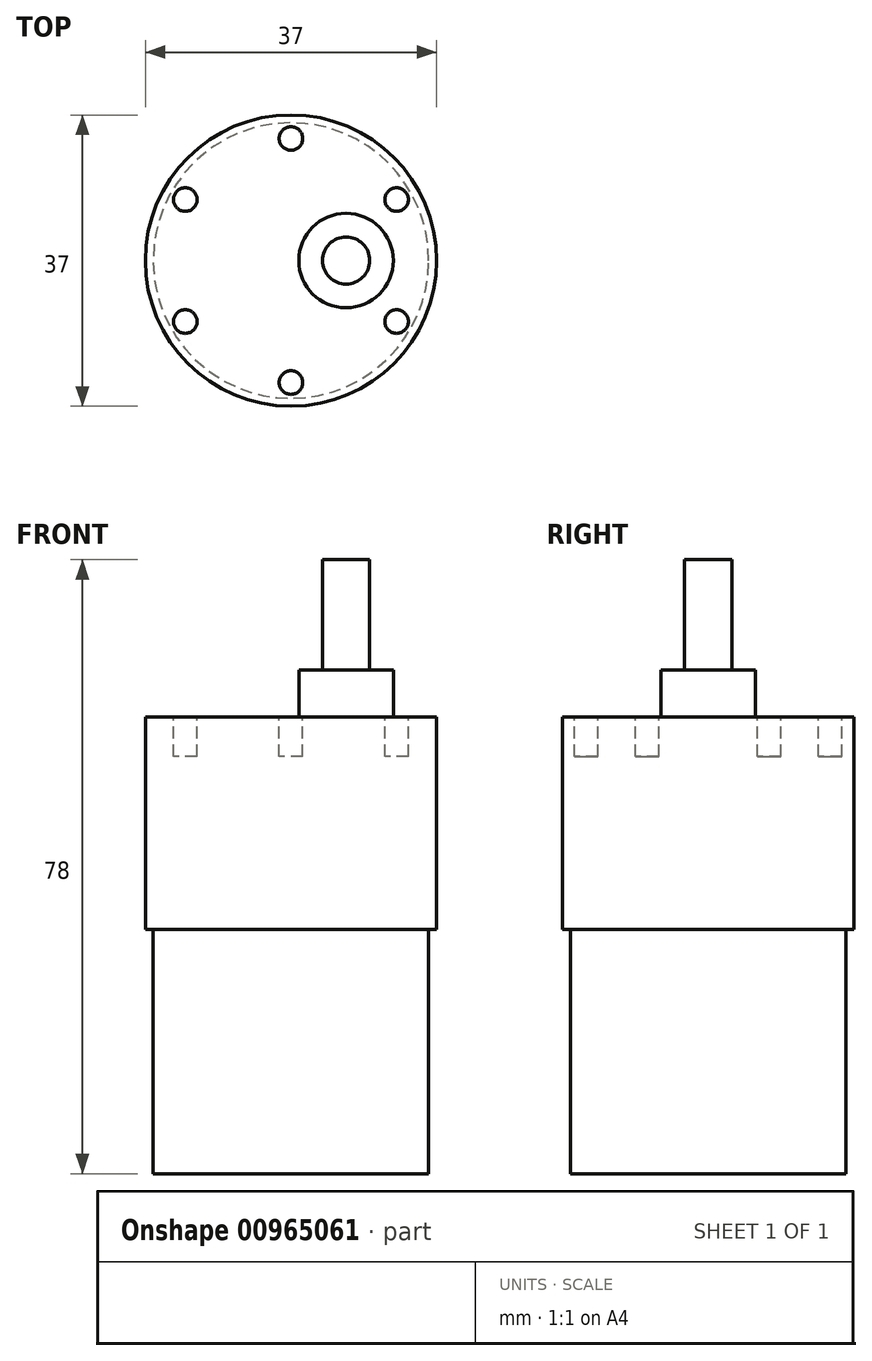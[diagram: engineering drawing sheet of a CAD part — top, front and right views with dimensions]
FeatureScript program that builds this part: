
annotation { "Feature Type Name" : "Feature", "Feature Type Description" : "" }
export const myFeature = defineFeature(function(context is Context, id is Id, definition is map)
    precondition{}
    {
        {
            var Q0;
            Q0=qCreatedBy(makeId("Top.planeOp"),FACE);
            var sketch = newSketch(context, id + "F0", { "sketchPlane" : qUnion([Q0])});
            skCircle(sketch, "E0", {"center": v(0, 0) * mm, "radius": 18.5 * mm});
            skCircle(sketch, "E1", {"center": v(0, 0) * mm, "radius": 17.5 * mm});
            skSolve(sketch);
        }
        {
            var Q0;
            Q0=makeQuery(id+"F0.imprint","IMPRINT",FACE,{"disambiguationData":[TD([[makeQuery(id+"F0.imprint","IMPRINT",EDGE,{"derivedFrom":sQuery(id+"F0.wireOp",EDGE,"E0")}),1.0]])]});
            var Q1;
            Q1=makeQuery(id+"F0.imprint","IMPRINT",FACE,{"disambiguationData":[TD([[makeQuery(id+"F0.imprint","IMPRINT",EDGE,{"derivedFrom":sQuery(id+"F0.wireOp",EDGE,"E1")}),1.0]])]});
            extrude(context, id + "F1", {"entities" : qUnion([Q0, Q1]), "flatOperationType" : FlatOperationType.REMOVE, "depth" : 27 * mm, "offsetDistance" : 25 * mm, "domain" : OperationDomain.MODEL});
        }
        {
            var Q0;
            Q0=makeQuery(id+"F0.imprint","IMPRINT",FACE,{"disambiguationData":[TD([[makeQuery(id+"F0.imprint","IMPRINT",EDGE,{"derivedFrom":sQuery(id+"F0.wireOp",EDGE,"E1")}),1.0]])]});
            extrude(context, id + "F2", {"entities" : qUnion([Q0]), "operationType" : NewBodyOperationType.ADD, "oppositeDirection" : true, "depth" : 31 * mm, "offsetDistance" : 25 * mm});
        }
        {
            var Q0;
            Q0=makeQuery(id+"F1.opExtrude","CAP_FACE",FACE,{"disambiguationData":[OSD([sQuery(id+"F0.wireOp",EDGE,"E0")])],"isStart":false});
            var sketch = newSketch(context, id + "F3", { "sketchPlane" : qUnion([Q0])});
            skCircle(sketch, "E2", {"center": v(0, 0) * mm, "radius": 13 * mm});
            skCircle(sketch, "E3", {"center": v(0, 15.5) * mm, "radius": 1.5 * mm});
            skCircle(sketch, "E4.1.0", {"center": v(-13.42, 7.75) * mm, "radius": 1.5 * mm});
            skCircle(sketch, "E4.2.0", {"center": v(-13.42, -7.75) * mm, "radius": 1.5 * mm});
            skCircle(sketch, "E4.3.0", {"center": v(0, -15.5) * mm, "radius": 1.5 * mm});
            skCircle(sketch, "E4.4.0", {"center": v(13.42, -7.75) * mm, "radius": 1.5 * mm});
            skCircle(sketch, "E4.5.0", {"center": v(13.42, 7.75) * mm, "radius": 1.5 * mm});
            skCircle(sketch, "E5", {"center": v(7, 0) * mm, "radius": 6 * mm});
            skCircle(sketch, "E6", {"center": v(7, 0) * mm, "radius": 3 * mm});
            skSolve(sketch);
        }
        {
            var Q0;
            Q0=makeQuery(id+"F3.imprint","IMPRINT",FACE,{"disambiguationData":[TD([[makeQuery(id+"F3.imprint","IMPRINT",EDGE,{"derivedFrom":sQuery(id+"F3.wireOp",EDGE,"E3")}),1.0]])]});
            var Q1;
            Q1=makeQuery(id+"F3.imprint","IMPRINT",FACE,{"disambiguationData":[TD([[makeQuery(id+"F3.imprint","IMPRINT",EDGE,{"derivedFrom":sQuery(id+"F3.wireOp",EDGE,"E4.5.0")}),1.0]])]});
            var Q2;
            Q2=makeQuery(id+"F3.imprint","IMPRINT",FACE,{"disambiguationData":[TD([[makeQuery(id+"F3.imprint","IMPRINT",EDGE,{"derivedFrom":sQuery(id+"F3.wireOp",EDGE,"E4.4.0")}),1.0]])]});
            var Q3;
            Q3=makeQuery(id+"F3.imprint","IMPRINT",FACE,{"disambiguationData":[TD([[makeQuery(id+"F3.imprint","IMPRINT",EDGE,{"derivedFrom":sQuery(id+"F3.wireOp",EDGE,"E4.3.0")}),1.0]])]});
            var Q4;
            Q4=makeQuery(id+"F3.imprint","IMPRINT",FACE,{"disambiguationData":[TD([[makeQuery(id+"F3.imprint","IMPRINT",EDGE,{"derivedFrom":sQuery(id+"F3.wireOp",EDGE,"E4.2.0")}),1.0]])]});
            var Q5;
            Q5=makeQuery(id+"F3.imprint","IMPRINT",FACE,{"disambiguationData":[TD([[makeQuery(id+"F3.imprint","IMPRINT",EDGE,{"derivedFrom":sQuery(id+"F3.wireOp",EDGE,"E4.1.0")}),1.0]])]});
            extrude(context, id + "F4", {"entities" : qUnion([Q0, Q1, Q2, Q3, Q4, Q5]), "operationType" : NewBodyOperationType.REMOVE, "oppositeDirection" : true, "depth" : 5 * mm, "offsetDistance" : 25 * mm});
        }
        {
            var Q0;
            Q0=makeQuery(id+"F3.imprint","IMPRINT",FACE,{"disambiguationData":[TD([[makeQuery(id+"F3.imprint","IMPRINT",EDGE,{"derivedFrom":sQuery(id+"F3.wireOp",EDGE,"E5")}),1.0]])]});
            extrude(context, id + "F5", {"entities" : qUnion([Q0]), "operationType" : NewBodyOperationType.ADD, "flatOperationType" : FlatOperationType.REMOVE, "depth" : 6 * mm, "offsetDistance" : 25 * mm, "domain" : OperationDomain.MODEL});
        }
        {
            var Q0;
            Q0=makeQuery(id+"F5.boolean.opBoolean","SPLIT",FACE,{"disambiguationData":[TD([makeQuery(id+"F5.opExtrude","SWEPT_FACE",FACE,{"disambiguationData":[OSD([sQuery(id+"F3.wireOp",EDGE,"E6")])]})])],"derivedFrom":makeQuery(id+"F1.opExtrude","CAP_FACE",FACE,{"disambiguationData":[OSD([sQuery(id+"F0.wireOp",EDGE,"E0")])],"isStart":false})});
            extrude(context, id + "F6", {"entities" : qUnion([Q0]), "operationType" : NewBodyOperationType.ADD, "depth" : 20 * mm, "offsetDistance" : 25 * mm});
        }
    });
